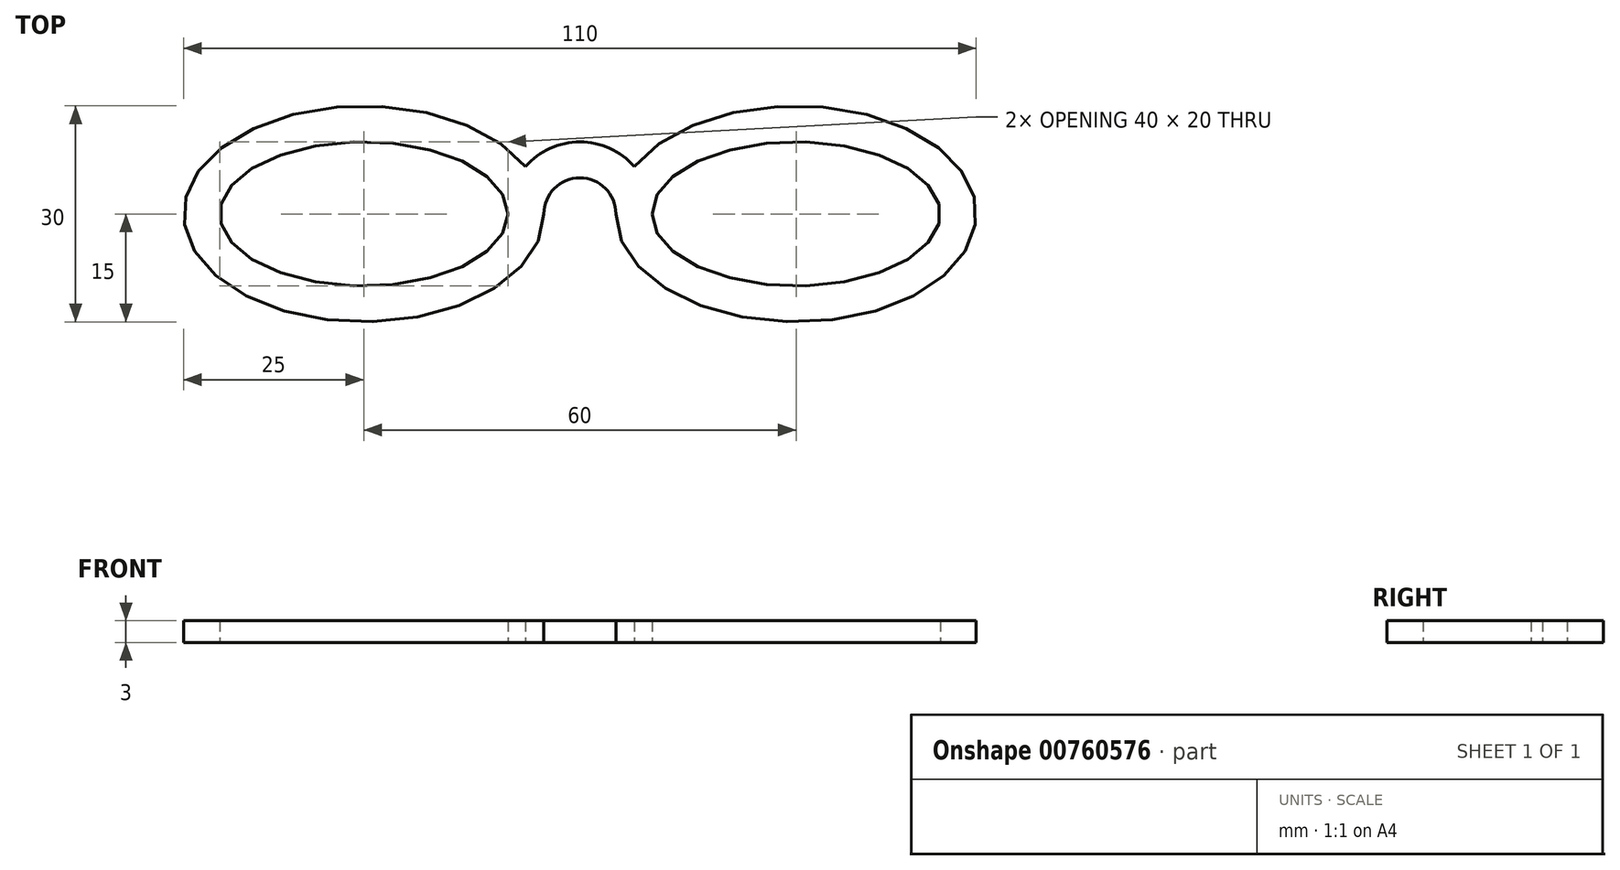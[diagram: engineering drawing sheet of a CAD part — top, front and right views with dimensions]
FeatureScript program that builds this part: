
annotation { "Feature Type Name" : "Feature", "Feature Type Description" : "" }
export const myFeature = defineFeature(function(context is Context, id is Id, definition is map)
    precondition{}
    {
        {
            var Q0;
            Q0=qCreatedBy(makeId("Top.planeOp"),FACE);
            var sketch = newSketch(context, id + "F0", { "sketchPlane" : qUnion([Q0])});
            skEllipse(sketch, "E0", {"center": v(-30, 0) * mm, "majorRadius": 20 * mm, "minorRadius": 10 * mm, "majorAxis": v(1, 0)});
            skEllipticalArc(sketch, "E1", {});
            skArc(sketch, "E2", {"start": v(5, 0) * mm, "mid": v(0, 5) * mm, "end": v(-5, 0) * mm});
            skArc(sketch, "E3", {"start": v(7.53, 6.58) * mm, "mid": v(0, 10) * mm, "end": v(-7.53, 6.58) * mm});
            skPoint(sketch, "E4.orphan", {"position": v(-10, 0) * mm});
            skEllipse(sketch, "E5.MirrorC", {"center": v(30, 0) * mm, "majorRadius": 20 * mm, "minorRadius": 10 * mm, "majorAxis": v(-1, 0)});
            skEllipticalArc(sketch, "E6.MirrorCS", {});
            skPoint(sketch, "E7.orphan", {"position": v(10, 0) * mm});
            const initialGuessF0  = {"E1": [-0.03, 0, 1, 0, 0.025, 0.015, 0.45395724671541643, 0], "E6.MirrorCS": [0.03, 0, -1, 0, 0.025, 0.015, 0, 5.82922806046417]};
            skSetInitialGuess(sketch, initialGuessF0);
            skSolve(sketch);
        }
        {
            var Q0;
            Q0 = qSketchRegion(id + "F0", true);
            extrude(context, id + "F1", {"entities" : qUnion([Q0]), "depth" : 3 * mm, "offsetDistance" : 25 * mm});
        }
    });
